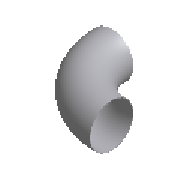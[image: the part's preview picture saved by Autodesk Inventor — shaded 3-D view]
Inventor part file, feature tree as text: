
AUTODESK INVENTOR PART (.ipt)
format: ipt  version: 2025 (Build 290162010, 162A)  size: 180,224 bytes
history: native  units: mm (DEFAULTED — no unit token found)
features: other x4, sweep x1
ambient origin geometry x8: Origin, YZ Plane, XZ Plane, XY Plane, X Axis, Y Axis, Z Axis, Center Point
bodies: Solid1 (feature_tree)
feature tree (5):
  sweep  "Sweep1"
  other  "Work Point1"
  other  "Work Axis1"
  other  "Work Point2"
  other  "Work Axis2"
